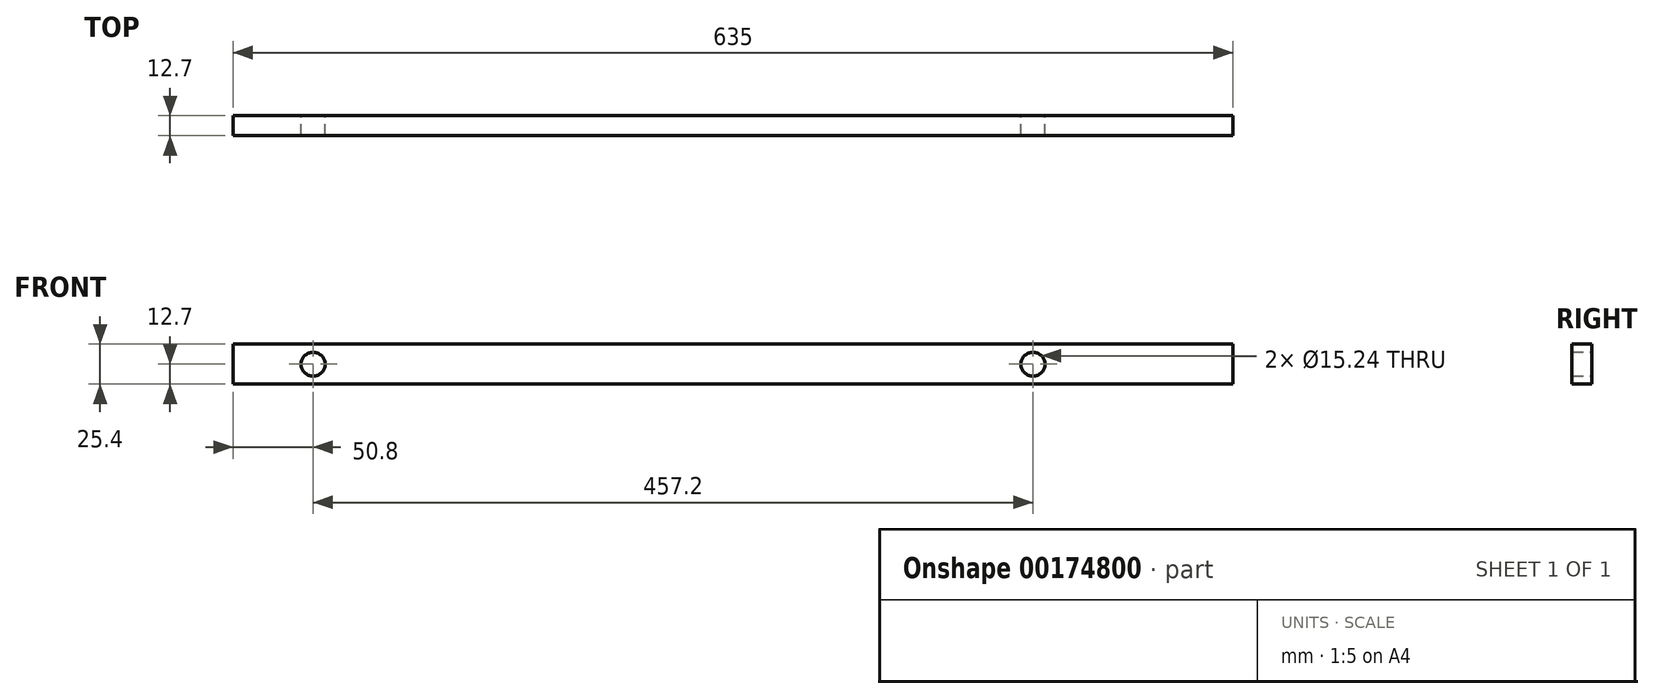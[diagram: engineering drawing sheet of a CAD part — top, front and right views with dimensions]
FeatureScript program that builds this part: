
annotation { "Feature Type Name" : "Feature", "Feature Type Description" : "" }
export const myFeature = defineFeature(function(context is Context, id is Id, definition is map)
    precondition{}
    {
        {
            var Q0;
            Q0=qCreatedBy(makeId("Front.planeOp"),FACE);
            var sketch = newSketch(context, id + "F0", { "sketchPlane" : qUnion([Q0])});
            skLineSegment(sketch, "E0.bottom", {"start": v(317.5, -12.7) * mm, "end": v(-317.5, -12.7) * mm});
            skLineSegment(sketch, "E0.top", {"start": v(317.5, 12.7) * mm, "end": v(-317.5, 12.7) * mm});
            skLineSegment(sketch, "E0.left", {"start": v(317.5, -12.7) * mm, "end": v(317.5, 12.7) * mm});
            skLineSegment(sketch, "E0.right", {"start": v(-317.5, -12.7) * mm, "end": v(-317.5, 12.7) * mm});
            skPoint(sketch, "E0.middle", {"position": v(0, 0) * mm});
            skCircle(sketch, "E1", {"center": v(-266.7, 0) * mm, "radius": 7.62 * mm});
            skCircle(sketch, "E2", {"center": v(190.5, 0) * mm, "radius": 7.62 * mm});
            skPoint(sketch, "E3.trimOffspring.end.orphan", {"position": v(317.5, 0) * mm});
            skPoint(sketch, "E4.start.orphan", {"position": v(-317.5, 0) * mm});
            skSolve(sketch);
        }
        {
            var Q0;
            Q0 = qSketchRegion(id + "F0", true);
            extrude(context, id + "F1", {"entities" : qUnion([Q0]), "depth" : 12.7 * mm});
        }
    });
